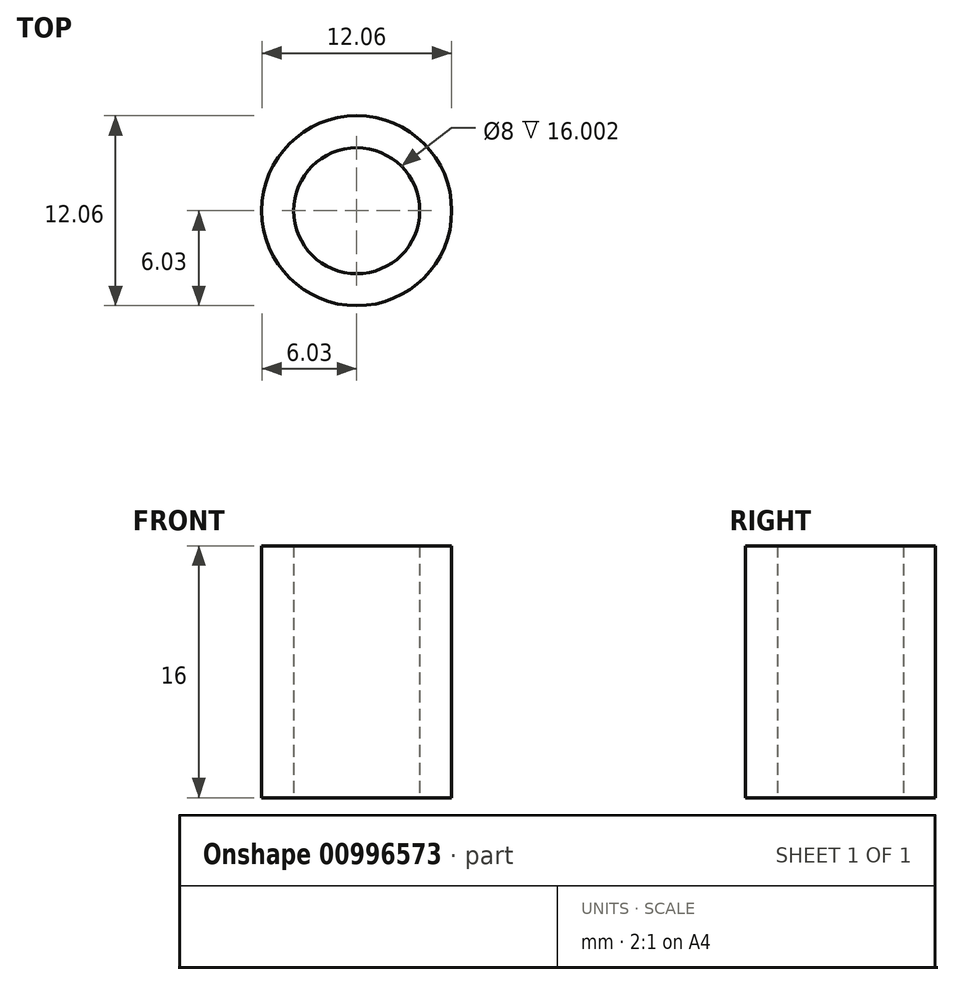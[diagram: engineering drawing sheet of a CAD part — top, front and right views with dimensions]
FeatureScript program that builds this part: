
annotation { "Feature Type Name" : "Feature", "Feature Type Description" : "" }
export const myFeature = defineFeature(function(context is Context, id is Id, definition is map)
    precondition{}
    {
        {
            var Q0;
            Q0=qCreatedBy(makeId("Top.planeOp"),FACE);
            var sketch = newSketch(context, id + "F0", { "sketchPlane" : qUnion([Q0])});
            skCircle(sketch, "E0", {"center": v(0, 0) * mm, "radius": 4 * mm});
            skCircle(sketch, "E1", {"center": v(0, 0) * mm, "radius": 6.03 * mm});
            skSolve(sketch);
        }
        {
            var Q0;
            Q0=qSketchRegion(id+"F0",true);
            extrude(context, id + "F1", {"entities" : qUnion([Q0]), "depth" : 16 * mm});
        }
    });
